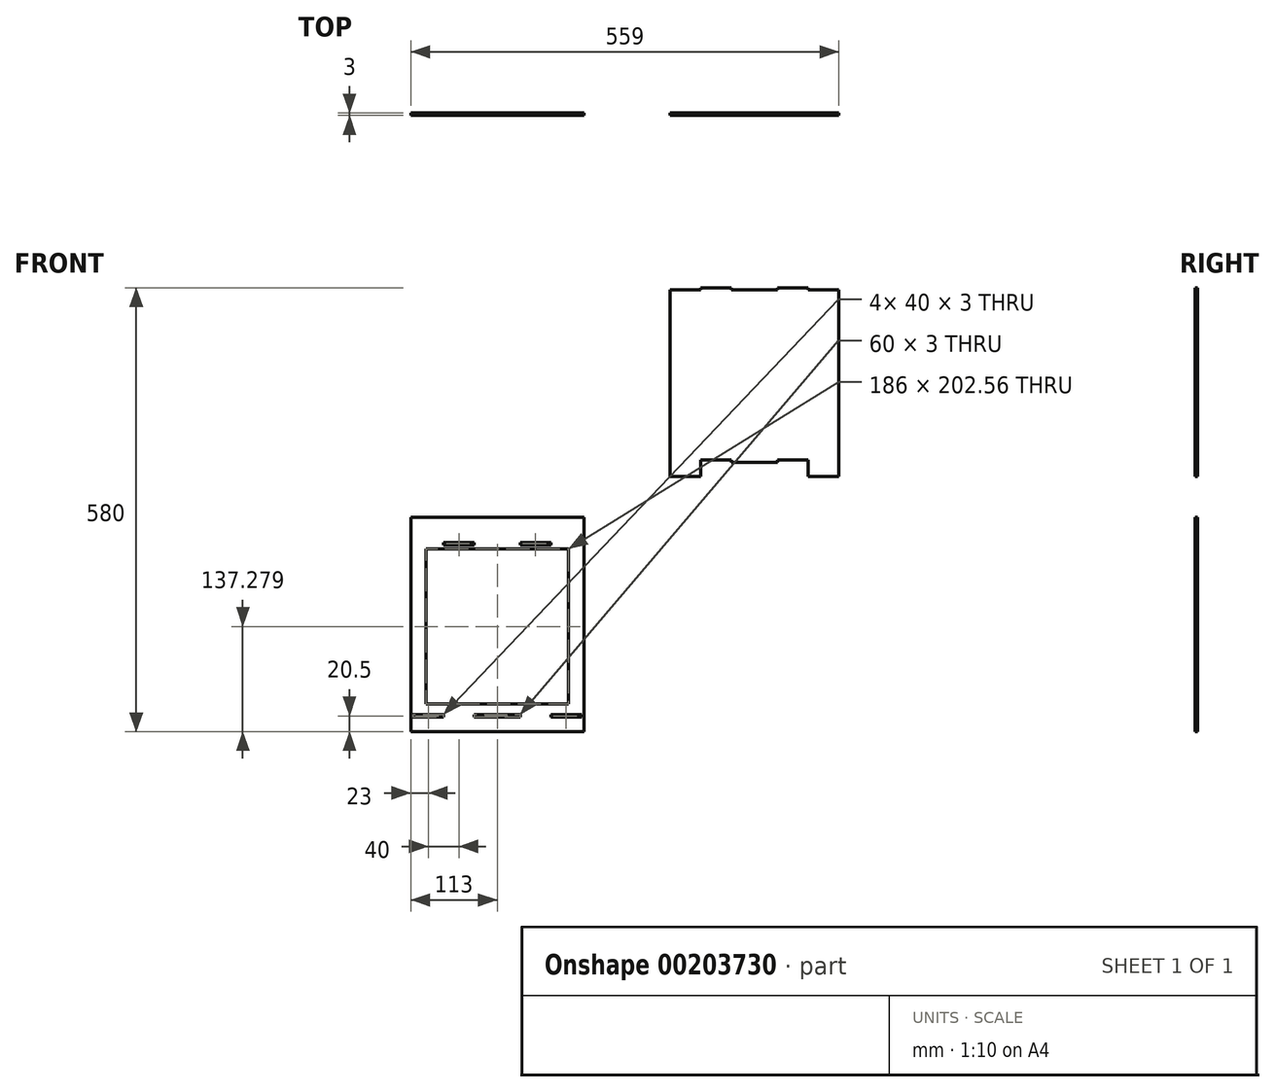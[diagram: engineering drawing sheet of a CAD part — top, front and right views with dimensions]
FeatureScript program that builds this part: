
annotation { "Feature Type Name" : "Feature", "Feature Type Description" : "" }
export const myFeature = defineFeature(function(context is Context, id is Id, definition is map)
    precondition{}
    {
        {
            var Q0;
            Q0=qCreatedBy(makeId("Front.planeOp"),FACE);
            var sketch = newSketch(context, id + "F0", { "sketchPlane" : qUnion([Q0])});
            skLineSegment(sketch, "E0.bottom", {"start": v(-110, 140) * mm, "end": v(110, 140) * mm});
            skLineSegment(sketch, "E0.top", {"start": v(-110, -140) * mm, "end": v(-70, -140) * mm});
            skLineSegment(sketch, "E0.left", {"start": v(-110, 140) * mm, "end": v(-110, -140) * mm});
            skLineSegment(sketch, "E0.right", {"start": v(110, 140) * mm, "end": v(110, -140) * mm});
            skPoint(sketch, "E0.middle", {"position": v(0, 0) * mm});
            skPoint(sketch, "E1", {"position": v(-110, 107) * mm});
            skLineSegment(sketch, "E2", {"start": v(-70, 107) * mm, "end": v(-30, 107) * mm});
            skLineSegment(sketch, "E3", {"start": v(-110, 104) * mm, "end": v(-93, 104) * mm});
            skPoint(sketch, "E4", {"position": v(-110, -118) * mm});
            skLineSegment(sketch, "E5", {"start": v(-70, -118) * mm, "end": v(-70, -121) * mm});
            skLineSegment(sketch, "E6", {"start": v(0, -140) * mm, "end": v(0, -118) * mm, "construction": true});
            skLineSegment(sketch, "E7.MirrorCS", {"start": v(70, -118) * mm, "end": v(70, -121) * mm});
            skLineSegment(sketch, "E8", {"start": v(-30, -121) * mm, "end": v(-30, -118) * mm});
            skLineSegment(sketch, "E9.MirrorCS", {"start": v(30, -121) * mm, "end": v(30, -118) * mm});
            skLineSegment(sketch, "E10", {"start": v(-70, 104) * mm, "end": v(-70, 107) * mm});
            skLineSegment(sketch, "E11", {"start": v(-30, 104) * mm, "end": v(-30, 107) * mm});
            skLineSegment(sketch, "E12", {"start": v(30, 104) * mm, "end": v(30, 107) * mm});
            skLineSegment(sketch, "E13", {"start": v(70, 104) * mm, "end": v(70, 107) * mm});
            skLineSegment(sketch, "E14.trimOffspring", {"start": v(-30, -140) * mm, "end": v(30, -140) * mm});
            skLineSegment(sketch, "E15.trimOffspring", {"start": v(70, -140) * mm, "end": v(110, -140) * mm});
            skLineSegment(sketch, "E16.trimOffspring", {"start": v(30, 107) * mm, "end": v(70, 107) * mm});
            skPoint(sketch, "E17.orphan", {"position": v(110, 107) * mm});
            skLineSegment(sketch, "E18.trimOffspring", {"start": v(93, 104) * mm, "end": v(110, 104) * mm});
            skPoint(sketch, "E19.orphan", {"position": v(110, -118) * mm});
            skLineSegment(sketch, "E20.bottom", {"start": v(113, 140) * mm, "end": v(-113, 140) * mm});
            skLineSegment(sketch, "E20.top", {"start": v(113, -140) * mm, "end": v(-113, -140) * mm});
            skLineSegment(sketch, "E20.left", {"start": v(113, 140) * mm, "end": v(113, -140) * mm});
            skLineSegment(sketch, "E20.right", {"start": v(-113, 140) * mm, "end": v(-113, -140) * mm});
            skLineSegment(sketch, "E21", {"start": v(-110, -121) * mm, "end": v(-70, -121) * mm});
            skLineSegment(sketch, "E22.trimOffspring", {"start": v(-30, -121) * mm, "end": v(30, -121) * mm});
            skLineSegment(sketch, "E23.trimOffspring", {"start": v(70, -121) * mm, "end": v(110, -121) * mm});
            skLineSegment(sketch, "E24", {"start": v(-110, -104) * mm, "end": v(110, -104) * mm});
            skLineSegment(sketch, "E25", {"start": v(-110, -118) * mm, "end": v(-70, -118) * mm});
            skLineSegment(sketch, "E26.trimOffspring", {"start": v(-30, -118) * mm, "end": v(30, -118) * mm});
            skLineSegment(sketch, "E27.trimOffspring", {"start": v(70, -118) * mm, "end": v(110, -118) * mm});
            skLineSegment(sketch, "E28", {"start": v(-93, 104) * mm, "end": v(-93, -118) * mm});
            skLineSegment(sketch, "E29", {"start": v(93, 104) * mm, "end": v(93, -118) * mm});
            skLineSegment(sketch, "E30", {"start": v(-93, 98.56) * mm, "end": v(93, 98.56) * mm});
            skLineSegment(sketch, "E31", {"start": v(-70, 104) * mm, "end": v(-30, 104) * mm});
            skLineSegment(sketch, "E32.trimOffspring", {"start": v(30, 104) * mm, "end": v(70, 104) * mm});
            skLineSegment(sketch, "E33", {"start": v(-93, 104) * mm, "end": v(-70, 104) * mm});
            skLineSegment(sketch, "E34", {"start": v(-30, 104) * mm, "end": v(30, 104) * mm});
            skLineSegment(sketch, "E35", {"start": v(70, 104) * mm, "end": v(93, 104) * mm});
            skLineSegment(sketch, "E36", {"start": v(-70, -118) * mm, "end": v(-30, -118) * mm});
            skLineSegment(sketch, "E37", {"start": v(30, -118) * mm, "end": v(70, -118) * mm});
            skLineSegment(sketch, "E38", {"start": v(-70, -121) * mm, "end": v(-70, -140) * mm});
            skLineSegment(sketch, "E39", {"start": v(-30, -140) * mm, "end": v(-30, -121) * mm});
            skLineSegment(sketch, "E40", {"start": v(30, -121) * mm, "end": v(30, -140) * mm});
            skLineSegment(sketch, "E41", {"start": v(70, -121) * mm, "end": v(70, -140) * mm});
            skSolve(sketch);
        }
        {
            var Q0;
            {var subQ2=sQuery(id+"F0.wireOp",EDGE,"E0.top");Q0=makeQuery(id+"F0.imprint","IMPRINT",FACE,{"disambiguationData":[TD([[makeQuery(id+"F0.imprint","IMPRINT",EDGE,{"derivedFrom":subQ2}),1.0]])]});}
            var Q1;
            Q1=makeQuery(id+"F0.imprint","IMPRINT",FACE,{"disambiguationData":[TD([[makeQuery(id+"F0.imprint","IMPRINT",EDGE,{"derivedFrom":sQuery(id+"F0.wireOp",EDGE,"E2")}),-1.0]])]});
            var Q2;
            {var subQ5=sQuery(id+"F0.wireOp",EDGE,"E30");Q2=makeQuery(id+"F0.imprint","IMPRINT",FACE,{"disambiguationData":[TD([[makeQuery(id+"F0.imprint","IMPRINT",EDGE,{"derivedFrom":subQ5}),-1.0]])]});}
            var Q3;
            Q3=makeQuery(id+"F0.imprint","IMPRINT",FACE,{"disambiguationData":[TD([[makeQuery(id+"F0.imprint","IMPRINT",EDGE,{"derivedFrom":sQuery(id+"F0.wireOp",EDGE,"E26.trimOffspring")}),1.0]])]});
            var Q4;
            {var subQ0=sQuery(id+"F0.wireOp",EDGE,"E30");Q4=makeQuery(id+"F0.imprint","IMPRINT",FACE,{"disambiguationData":[TD([[makeQuery(id+"F0.imprint","IMPRINT",EDGE,{"derivedFrom":subQ0}),1.0]])]});}
            var Q5;
            Q5=makeQuery(id+"F0.imprint","IMPRINT",FACE,{"disambiguationData":[TD([[makeQuery(id+"F0.imprint","IMPRINT",EDGE,{"derivedFrom":sQuery(id+"F0.wireOp",EDGE,"E12")}),-1.0]])]});
            var Q6;
            {var subQ1=sQuery(id+"F0.wireOp",EDGE,"E3");Q6=makeQuery(id+"F0.imprint","IMPRINT",FACE,{"disambiguationData":[TD([[makeQuery(id+"F0.imprint","IMPRINT",EDGE,{"derivedFrom":subQ1}),-1.0]])]});}
            var Q7;
            {var subQ1=sQuery(id+"F0.wireOp",EDGE,"E18.trimOffspring");Q7=makeQuery(id+"F0.imprint","IMPRINT",FACE,{"disambiguationData":[TD([[makeQuery(id+"F0.imprint","IMPRINT",EDGE,{"derivedFrom":subQ1}),-1.0]])]});}
            var Q8;
            {var subQ0=sQuery(id+"F0.wireOp",EDGE,"E24");var subQ1=sQuery(id+"F0.wireOp",EDGE,"E0.left");var subQ2=makeQuery(id+"F0.imprint","INTERSECT",VERTEX,{"derivedFrom":[subQ1,subQ0]});Q8=makeQuery(id+"F0.imprint","IMPRINT",FACE,{"disambiguationData":[TD([[makeQuery(id+"F0.imprint","IMPRINT",EDGE,{"disambiguationData":[TD([[subQ2,-1.0]])],"derivedFrom":subQ1}),1.0]])]});}
            var Q9;
            {var subQ3=sQuery(id+"F0.wireOp",EDGE,"E21");Q9=makeQuery(id+"F0.imprint","IMPRINT",FACE,{"disambiguationData":[TD([[makeQuery(id+"F0.imprint","IMPRINT",EDGE,{"derivedFrom":subQ3}),-1.0]])]});}
            var Q10;
            {var subQ5=sQuery(id+"F0.wireOp",EDGE,"E5");Q10=makeQuery(id+"F0.imprint","IMPRINT",FACE,{"disambiguationData":[TD([[makeQuery(id+"F0.imprint","IMPRINT",EDGE,{"derivedFrom":subQ5}),-1.0]])]});}
            var Q11;
            Q11=makeQuery(id+"F0.imprint","IMPRINT",FACE,{"disambiguationData":[TD([[makeQuery(id+"F0.imprint","IMPRINT",EDGE,{"derivedFrom":sQuery(id+"F0.wireOp",EDGE,"E8")}),-1.0]])]});
            var Q12;
            {var subQ3=sQuery(id+"F0.wireOp",EDGE,"E23.trimOffspring");Q12=makeQuery(id+"F0.imprint","IMPRINT",FACE,{"disambiguationData":[TD([[makeQuery(id+"F0.imprint","IMPRINT",EDGE,{"derivedFrom":subQ3}),-1.0]])]});}
            var Q13;
            {var subQ2=sQuery(id+"F0.wireOp",EDGE,"E7.MirrorCS");Q13=makeQuery(id+"F0.imprint","IMPRINT",FACE,{"disambiguationData":[TD([[makeQuery(id+"F0.imprint","IMPRINT",EDGE,{"derivedFrom":subQ2}),1.0]])]});}
            var Q14;
            {var subQ0=sQuery(id+"F0.wireOp",EDGE,"E24");var subQ1=sQuery(id+"F0.wireOp",EDGE,"E0.right");var subQ2=makeQuery(id+"F0.imprint","INTERSECT",VERTEX,{"derivedFrom":[subQ1,subQ0]});Q14=makeQuery(id+"F0.imprint","IMPRINT",FACE,{"disambiguationData":[TD([[makeQuery(id+"F0.imprint","IMPRINT",EDGE,{"disambiguationData":[TD([[subQ2,-1.0]])],"derivedFrom":subQ1}),-1.0]])]});}
            extrude(context, id + "F1", {"entities" : qUnion([Q0, Q1, Q2, Q3, Q4, Q5, Q6, Q7, Q8, Q9, Q10, Q11, Q12, Q13, Q14]), "depth" : 3 * mm});
        }
        {
            var Q0;
            Q0=makeQuery(id+"F1.opExtrude","SWEPT_BODY",BODY,{"disambiguationData":[OSD([sQuery(id+"F0.wireOp",EDGE,"E0.left"),sQuery(id+"F0.wireOp",EDGE,"E0.right"),sQuery(id+"F0.wireOp",EDGE,"E2"),sQuery(id+"F0.wireOp",EDGE,"E3"),sQuery(id+"F0.wireOp",EDGE,"fNa47I4L-dXQQ-Sxzq-Cwo6-yq2eIPETGIAt"),sQuery(id+"F0.wireOp",EDGE,"E5"),sQuery(id+"F0.wireOp",EDGE,"E7.MirrorCS"),sQuery(id+"F0.wireOp",EDGE,"E8"),sQuery(id+"F0.wireOp",EDGE,"E9.MirrorCS"),sQuery(id+"F0.wireOp",EDGE,"E10"),sQuery(id+"F0.wireOp",EDGE,"E11"),sQuery(id+"F0.wireOp",EDGE,"E12"),sQuery(id+"F0.wireOp",EDGE,"E13"),sQuery(id+"F0.wireOp",EDGE,"E16.trimOffspring"),sQuery(id+"F0.wireOp",EDGE,"E18.trimOffspring"),sQuery(id+"F0.wireOp",EDGE,"66d02d63-2e19-4b06-a3f9-a3e4b8704bff.trimOffspring"),sQuery(id+"F0.wireOp",EDGE,"eac27a3a-007c-41c9-90df-22aec6e10a82.trimOffspring"),sQuery(id+"F0.wireOp",EDGE,"E20.top")])]});
            transform(context, id + "F2", {"entities" : qUnion([Q0]), "transformType" : TransformType.TRANSLATION_3D, "dx" : 336 * mm, "dy" : 0 * mm, "dz" : 0 * mm, "makeCopy" : false});
        }
        {
            var Q0;
            Q0=makeQuery(id+"F0.imprint","IMPRINT",FACE,{"disambiguationData":[TD([[makeQuery(id+"F0.imprint","IMPRINT",EDGE,{"derivedFrom":sQuery(id+"F0.wireOp",EDGE,"fNa47I4L-dXQQ-Sxzq-Cwo6-yq2eIPETGIAt")}),-1.0]])]});
            var Q1;
            {var subQ3=sQuery(id+"F0.wireOp",EDGE,"E20.right");Q1=makeQuery(id+"F0.imprint","IMPRINT",FACE,{"disambiguationData":[TD([[makeQuery(id+"F0.imprint","IMPRINT",EDGE,{"derivedFrom":subQ3}),1.0]])]});}
            var Q2;
            Q2=makeQuery(id+"F0.imprint","IMPRINT",FACE,{"disambiguationData":[TD([[makeQuery(id+"F0.imprint","IMPRINT",EDGE,{"derivedFrom":sQuery(id+"F0.wireOp",EDGE,"E2")}),1.0]])]});
            var Q3;
            {var subQ3=sQuery(id+"F0.wireOp",EDGE,"E20.left");Q3=makeQuery(id+"F0.imprint","IMPRINT",FACE,{"disambiguationData":[TD([[makeQuery(id+"F0.imprint","IMPRINT",EDGE,{"derivedFrom":subQ3}),-1.0]])]});}
            var Q4;
            Q4=makeQuery(id+"F0.imprint","IMPRINT",FACE,{"disambiguationData":[TD([[makeQuery(id+"F0.imprint","IMPRINT",EDGE,{"derivedFrom":sQuery(id+"F0.wireOp",EDGE,"E5")}),1.0]])]});
            var Q5;
            {var subQ1=sQuery(id+"F0.wireOp",EDGE,"E3");Q5=makeQuery(id+"F0.imprint","IMPRINT",FACE,{"disambiguationData":[TD([[makeQuery(id+"F0.imprint","IMPRINT",EDGE,{"derivedFrom":subQ1}),-1.0]])]});}
            var Q6;
            {var subQ0=sQuery(id+"F0.wireOp",EDGE,"E24");var subQ1=sQuery(id+"F0.wireOp",EDGE,"E0.left");var subQ2=makeQuery(id+"F0.imprint","INTERSECT",VERTEX,{"derivedFrom":[subQ1,subQ0]});Q6=makeQuery(id+"F0.imprint","IMPRINT",FACE,{"disambiguationData":[TD([[makeQuery(id+"F0.imprint","IMPRINT",EDGE,{"disambiguationData":[TD([[subQ2,-1.0]])],"derivedFrom":subQ1}),1.0]])]});}
            var Q7;
            {var subQ0=sQuery(id+"F0.wireOp",EDGE,"E24");var subQ1=sQuery(id+"F0.wireOp",EDGE,"E0.right");var subQ2=makeQuery(id+"F0.imprint","INTERSECT",VERTEX,{"derivedFrom":[subQ1,subQ0]});Q7=makeQuery(id+"F0.imprint","IMPRINT",FACE,{"disambiguationData":[TD([[makeQuery(id+"F0.imprint","IMPRINT",EDGE,{"disambiguationData":[TD([[subQ2,-1.0]])],"derivedFrom":subQ1}),-1.0]])]});}
            var Q8;
            {var subQ1=sQuery(id+"F0.wireOp",EDGE,"E18.trimOffspring");Q8=makeQuery(id+"F0.imprint","IMPRINT",FACE,{"disambiguationData":[TD([[makeQuery(id+"F0.imprint","IMPRINT",EDGE,{"derivedFrom":subQ1}),-1.0]])]});}
            var Q9;
            {var subQ3=sQuery(id+"F0.wireOp",EDGE,"E21");Q9=makeQuery(id+"F0.imprint","IMPRINT",FACE,{"disambiguationData":[TD([[makeQuery(id+"F0.imprint","IMPRINT",EDGE,{"derivedFrom":subQ3}),-1.0]])]});}
            var Q10;
            Q10=makeQuery(id+"F0.imprint","IMPRINT",FACE,{"disambiguationData":[TD([[makeQuery(id+"F0.imprint","IMPRINT",EDGE,{"derivedFrom":sQuery(id+"F0.wireOp",EDGE,"E22.trimOffspring")}),-1.0]])]});
            var Q11;
            Q11=makeQuery(id+"F0.imprint","IMPRINT",FACE,{"disambiguationData":[TD([[makeQuery(id+"F0.imprint","IMPRINT",EDGE,{"derivedFrom":sQuery(id+"F0.wireOp",EDGE,"E7.MirrorCS")}),-1.0]])]});
            var Q12;
            {var subQ3=sQuery(id+"F0.wireOp",EDGE,"E23.trimOffspring");Q12=makeQuery(id+"F0.imprint","IMPRINT",FACE,{"disambiguationData":[TD([[makeQuery(id+"F0.imprint","IMPRINT",EDGE,{"derivedFrom":subQ3}),-1.0]])]});}
            var Q13;
            Q13=makeQuery(id+"F0.imprint","IMPRINT",FACE,{"disambiguationData":[TD([[makeQuery(id+"F0.imprint","IMPRINT",EDGE,{"derivedFrom":sQuery(id+"F0.wireOp",EDGE,"E26.trimOffspring")}),1.0]])]});
            var Q14;
            {var subQ0=sQuery(id+"F0.wireOp",EDGE,"E30");Q14=makeQuery(id+"F0.imprint","IMPRINT",FACE,{"disambiguationData":[TD([[makeQuery(id+"F0.imprint","IMPRINT",EDGE,{"derivedFrom":subQ0}),1.0]])]});}
            extrude(context, id + "F3", {"entities" : qUnion([Q0, Q1, Q2, Q3, Q4, Q5, Q6, Q7, Q8, Q9, Q10, Q11, Q12, Q13, Q14]), "depth" : 3 * mm});
        }
        {
            var Q0;
            Q0=makeQuery(id+"F3.opExtrude","SWEPT_BODY",BODY,{"disambiguationData":[OSD([sQuery(id+"F0.wireOp",EDGE,"E0.left"),sQuery(id+"F0.wireOp",EDGE,"E0.right"),sQuery(id+"F0.wireOp",EDGE,"E2"),sQuery(id+"F0.wireOp",EDGE,"E3"),sQuery(id+"F0.wireOp",EDGE,"fNa47I4L-dXQQ-Sxzq-Cwo6-yq2eIPETGIAt"),sQuery(id+"F0.wireOp",EDGE,"E5"),sQuery(id+"F0.wireOp",EDGE,"E7.MirrorCS"),sQuery(id+"F0.wireOp",EDGE,"E8"),sQuery(id+"F0.wireOp",EDGE,"E9.MirrorCS"),sQuery(id+"F0.wireOp",EDGE,"E10"),sQuery(id+"F0.wireOp",EDGE,"E11"),sQuery(id+"F0.wireOp",EDGE,"E12"),sQuery(id+"F0.wireOp",EDGE,"E13"),sQuery(id+"F0.wireOp",EDGE,"E16.trimOffspring"),sQuery(id+"F0.wireOp",EDGE,"E18.trimOffspring"),sQuery(id+"F0.wireOp",EDGE,"66d02d63-2e19-4b06-a3f9-a3e4b8704bff.trimOffspring"),sQuery(id+"F0.wireOp",EDGE,"eac27a3a-007c-41c9-90df-22aec6e10a82.trimOffspring"),sQuery(id+"F0.wireOp",EDGE,"E20.bottom"),sQuery(id+"F0.wireOp",EDGE,"E20.top"),sQuery(id+"F0.wireOp",EDGE,"E20.left"),sQuery(id+"F0.wireOp",EDGE,"E20.right"),sQuery(id+"F0.wireOp",EDGE,"E21"),sQuery(id+"F0.wireOp",EDGE,"E22.trimOffspring"),sQuery(id+"F0.wireOp",EDGE,"E23.trimOffspring")])]});
            transform(context, id + "F4", {"entities" : qUnion([Q0]), "transformType" : TransformType.TRANSLATION_3D, "dx" : 0 * mm, "dy" : 0 * mm, "dz" : -333 * mm, "makeCopy" : false});
        }
    });
